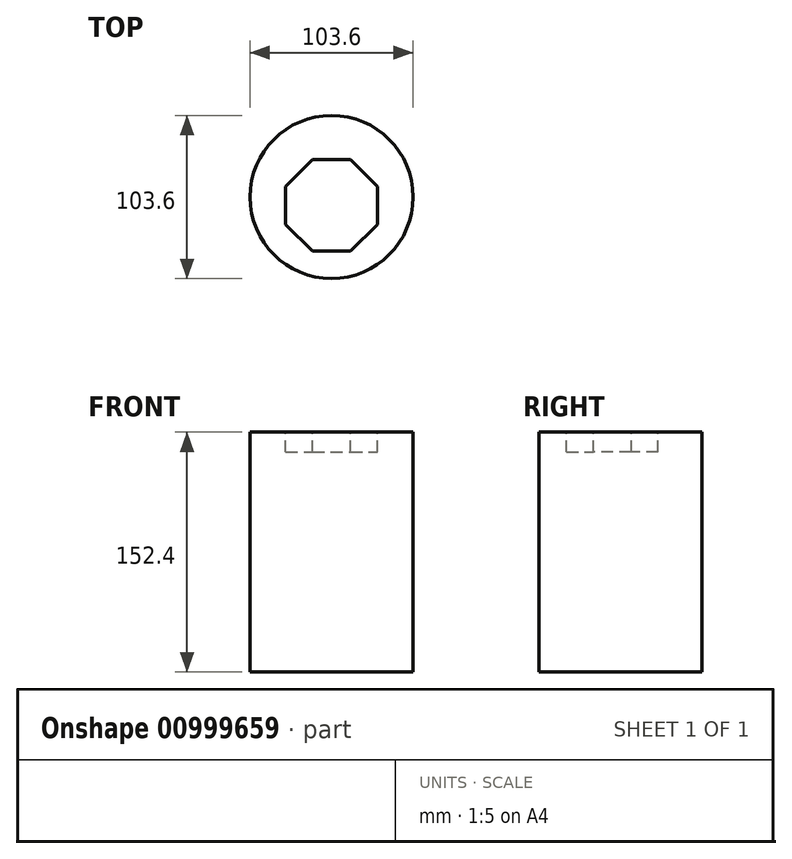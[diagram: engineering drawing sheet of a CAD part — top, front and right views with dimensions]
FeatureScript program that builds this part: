
annotation { "Feature Type Name" : "Feature", "Feature Type Description" : "" }
export const myFeature = defineFeature(function(context is Context, id is Id, definition is map)
    precondition{}
    {
        {
            var Q0;
            Q0=qCreatedBy(makeId("Top.planeOp"),FACE);
            var sketch = newSketch(context, id + "F0", { "sketchPlane" : qUnion([Q0])});
            skCircle(sketch, "E0", {"center": v(0, 0) * mm, "radius": 51.8 * mm});
            skSolve(sketch);
        }
        {
            var Q0;
            Q0=makeQuery(id+"F0.imprint","IMPRINT",FACE,{"disambiguationData":[TD([[makeQuery(id+"F0.imprint","IMPRINT",EDGE,{"derivedFrom":sQuery(id+"F0.wireOp",EDGE,"E0")}),1.0]])]});
            extrude(context, id + "F1", {"entities" : qUnion([Q0]), "depth" : 76.2 * mm, "offsetDistance" : 25.4 * mm});
        }
        {
            var Q0;
            Q0=makeQuery(id+"F1.opExtrude","CAP_FACE",FACE,{"disambiguationData":[OSD([sQuery(id+"F0.wireOp",EDGE,"E0")])],"isStart":false});
            extrude(context, id + "F2", {"entities" : qUnion([Q0]), "operationType" : NewBodyOperationType.REMOVE, "oppositeDirection" : true, "depth" : 25.4 * mm, "offsetDistance" : 25.4 * mm});
        }
        {
            var Q0;
            Q0=makeQuery(id+"F2.boolean.opBoolean","COPY",FACE,{"derivedFrom":makeQuery(id+"F2.opExtrude","CAP_FACE",FACE,{"disambiguationData":[OSD([sQuery(id+"F0.wireOp",EDGE,"E0")])],"isStart":false})});
            extrude(context, id + "F3", {"entities" : qUnion([Q0]), "operationType" : NewBodyOperationType.REMOVE, "oppositeDirection" : true, "depth" : 25.4 * mm, "offsetDistance" : 25.4 * mm});
        }
        {
            var Q0;
            Q0=makeQuery(id+"F3.boolean.opBoolean","COPY",FACE,{"derivedFrom":makeQuery(id+"F3.opExtrude","CAP_FACE",FACE,{"disambiguationData":[OSD([sQuery(id+"F0.wireOp",EDGE,"E0")])],"isStart":false})});
            var sketch = newSketch(context, id + "F4", { "sketchPlane" : qUnion([Q0])});
            skCircle(sketch, "E1.cCircle", {"center": v(0, -5.33) * mm, "radius": 29.1 * mm, "construction": true});
            skLineSegment(sketch, "E1.0", {"start": v(29.1, 6.72) * mm, "end": v(29.1, -17.38) * mm});
            skLineSegment(sketch, "E1.1", {"start": v(29.1, -17.38) * mm, "end": v(12.05, -34.42) * mm});
            skLineSegment(sketch, "E1.2", {"start": v(12.05, -34.42) * mm, "end": v(-12.05, -34.42) * mm});
            skLineSegment(sketch, "E1.3", {"start": v(-12.05, -34.42) * mm, "end": v(-29.1, -17.38) * mm});
            skLineSegment(sketch, "E1.4", {"start": v(-29.1, -17.38) * mm, "end": v(-29.1, 6.72) * mm});
            skLineSegment(sketch, "E1.5", {"start": v(-29.1, 6.72) * mm, "end": v(-12.05, 23.77) * mm});
            skLineSegment(sketch, "E1.6", {"start": v(-12.05, 23.77) * mm, "end": v(12.05, 23.77) * mm});
            skLineSegment(sketch, "E1.7", {"start": v(12.05, 23.77) * mm, "end": v(29.1, 6.72) * mm});
            skPoint(sketch, "E1.0.midPoint", {"position": v(29.1, -5.33) * mm});
            skSolve(sketch);
        }
        {
            var Q0;
            Q0=makeQuery(id+"F4.imprint","IMPRINT",FACE,{"disambiguationData":[TD([[makeQuery(id+"F4.imprint","IMPRINT",EDGE,{"derivedFrom":sQuery(id+"F4.wireOp",EDGE,"E1.0")}),-1.0]])]});
            extrude(context, id + "F5", {"entities" : qUnion([Q0]), "operationType" : NewBodyOperationType.REMOVE, "oppositeDirection" : true, "depth" : 12.7 * mm, "offsetDistance" : 25.4 * mm});
        }
        {
            var Q0;
            Q0=makeQuery(id+"F1.opExtrude","CAP_FACE",FACE,{"disambiguationData":[OSD([sQuery(id+"F0.wireOp",EDGE,"E0")])],"isStart":true});
            extrude(context, id + "F6", {"entities" : qUnion([Q0]), "operationType" : NewBodyOperationType.ADD, "depth" : 127 * mm, "offsetDistance" : 25.4 * mm});
        }
    });
